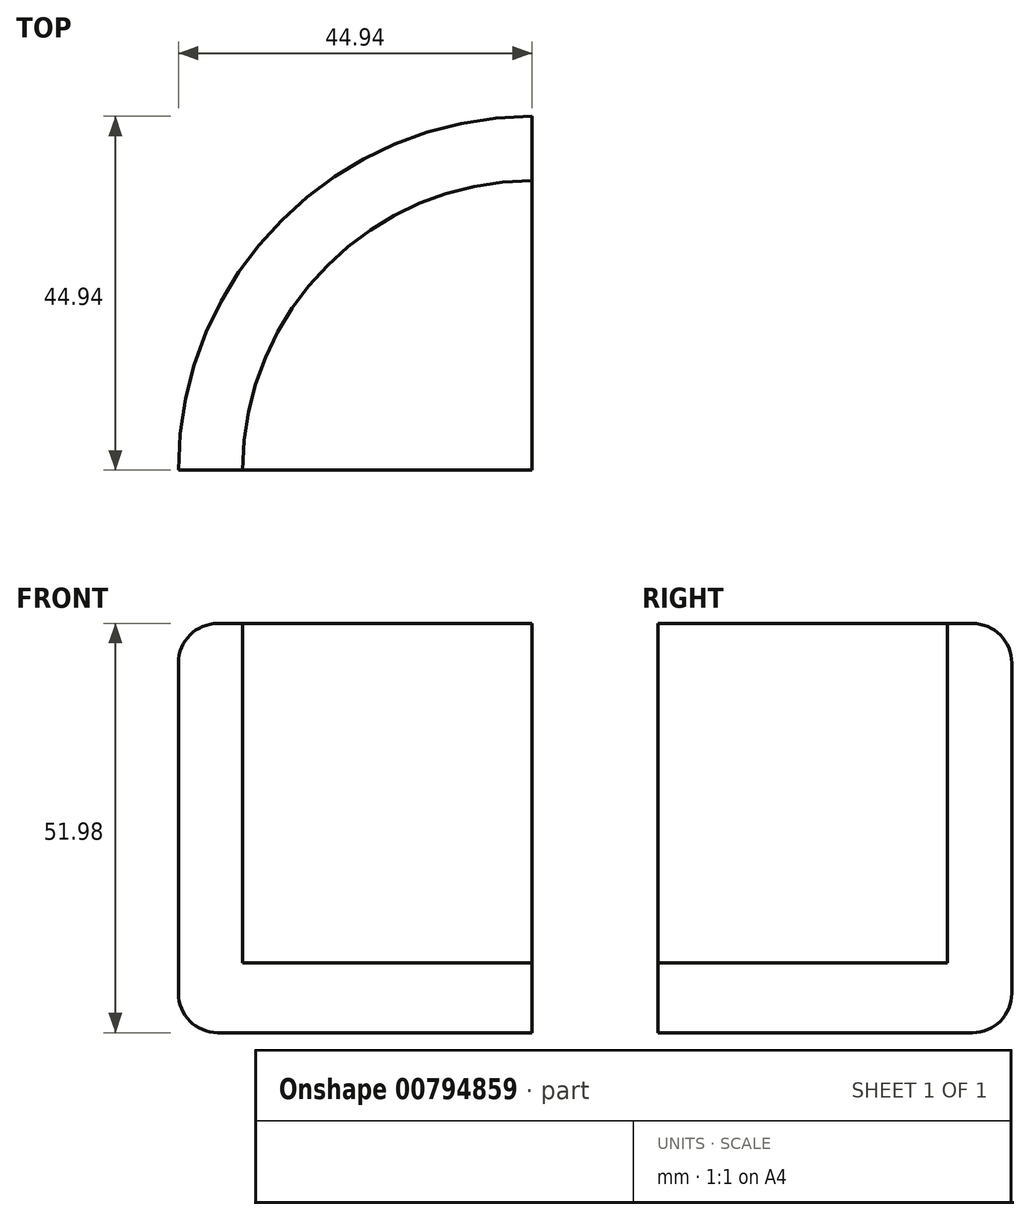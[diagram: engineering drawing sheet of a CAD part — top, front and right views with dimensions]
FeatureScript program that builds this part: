
annotation { "Feature Type Name" : "Feature", "Feature Type Description" : "" }
export const myFeature = defineFeature(function(context is Context, id is Id, definition is map)
    precondition{}
    {
        {
            var Q0;
            Q0=qCreatedBy(makeId("Front.planeOp"),FACE);
            var sketch = newSketch(context, id + "F0", { "sketchPlane" : qUnion([Q0])});
            skLineSegment(sketch, "E0", {"start": v(0, 0) * mm, "end": v(-44.94, 0) * mm});
            skLineSegment(sketch, "E1", {"start": v(-44.94, 0) * mm, "end": v(-44.94, 51.98) * mm});
            skLineSegment(sketch, "E2", {"start": v(-44.94, 51.98) * mm, "end": v(-36.77, 51.98) * mm});
            skLineSegment(sketch, "E3", {"start": v(-36.77, 51.98) * mm, "end": v(-36.77, 8.87) * mm});
            skLineSegment(sketch, "E4", {"start": v(-36.77, 8.87) * mm, "end": v(0, 8.87) * mm});
            skLineSegment(sketch, "E5", {"start": v(0, 8.87) * mm, "end": v(0, 0) * mm});
            skSolve(sketch);
        }
        {
            var Q0;
            Q0=makeQuery(id+"F0.imprint","IMPRINT",FACE,{"disambiguationData":[TD([[makeQuery(id+"F0.imprint","IMPRINT",EDGE,{"derivedFrom":sQuery(id+"F0.wireOp",EDGE,"E0")}),-1.0]])]});
            var Q1;
            Q1=sQuery(id+"F0.wireOp",EDGE,"E5");
            revolve(context, id + "F1", {"surfaceOperationType" : NewSurfaceOperationType.NEW, "entities" : qUnion([Q0]), "axis" : qUnion([Q1]), "revolveType" : RevolveType.ONE_DIRECTION, "angle" : 90 * degree});
        }
        {
            var Q0;
            Q0=makeQuery(id+"F1.opRevolve","SWEPT_EDGE",EDGE,{"disambiguationData":[OSD([sQuery(id+"F0.wireOp",EDGE,"E1"),sQuery(id+"F0.wireOp",EDGE,"E2")])]});
            var Q1;
            Q1=makeQuery(id+"F1.opRevolve","SWEPT_EDGE",EDGE,{"disambiguationData":[OSD([sQuery(id+"F0.wireOp",EDGE,"E0"),sQuery(id+"F0.wireOp",EDGE,"E1")])]});
            fillet(context, id + "F2", {"entities" : qUnion([Q0, Q1]), "radius" : 5 * mm, "tangentPropagation" : true, "allowEdgeOverflow" : false});
        }
    });
